# Revit family: SDD75x193
name_source: partatom
category: Structural Connections
revit_build: Autodesk Revit 2016 (Build: 20150220_1215(x64)
units: mm (PartAtom-declared; Revit-internal decimal feet)

## family parameters
Always vertical = No
Cut with Voids When Loaded = No
Enable cutting in views = No
Material for Model Behavior = Steel
OmniClass Number = 23.20.40.11.14.24
OmniClass Title = Screws
Shared = No
Work Plane-Based = Yes

## types (1)
- SDD75x193
    Default Elevation = 0 mm  [stored 0 ft]
    Density = 0.07 kg
    Description = Self-Drilling Dowel
    EPD = https://www.strongtie.eu
    ETA / DoP = https://www.strongtie.eu
    Manufacturer = Simpson Strong-Tie
    Model = SDD7.5x193
    Model Disclaimer = Contact Simpson Strong-Tie Company  for more information
    Model ID = 0308049226507827704599664298313210546978
    Name = SDD7.5x193
    ObjectType = SDD7.5x193
    Product Material = ElectroGalvanised
    Product Type = Self-Drilling Dowel
    Reference = SDD7.5X193
    Technical datasheet = https://www.strongtie.eu
    URL = www.strongtie.eu
    UniClass Number = Pr_20_29_76_98
    UniClass Title = Wood screws

note: [stored X ft] marks values corroborated as IEEE doubles in the binary element streams (Revit-internal decimal feet)

## geometry (parser evidence)
native form markers: Blend x25, Sweep x3
no freeform markers — native parametric forms only
